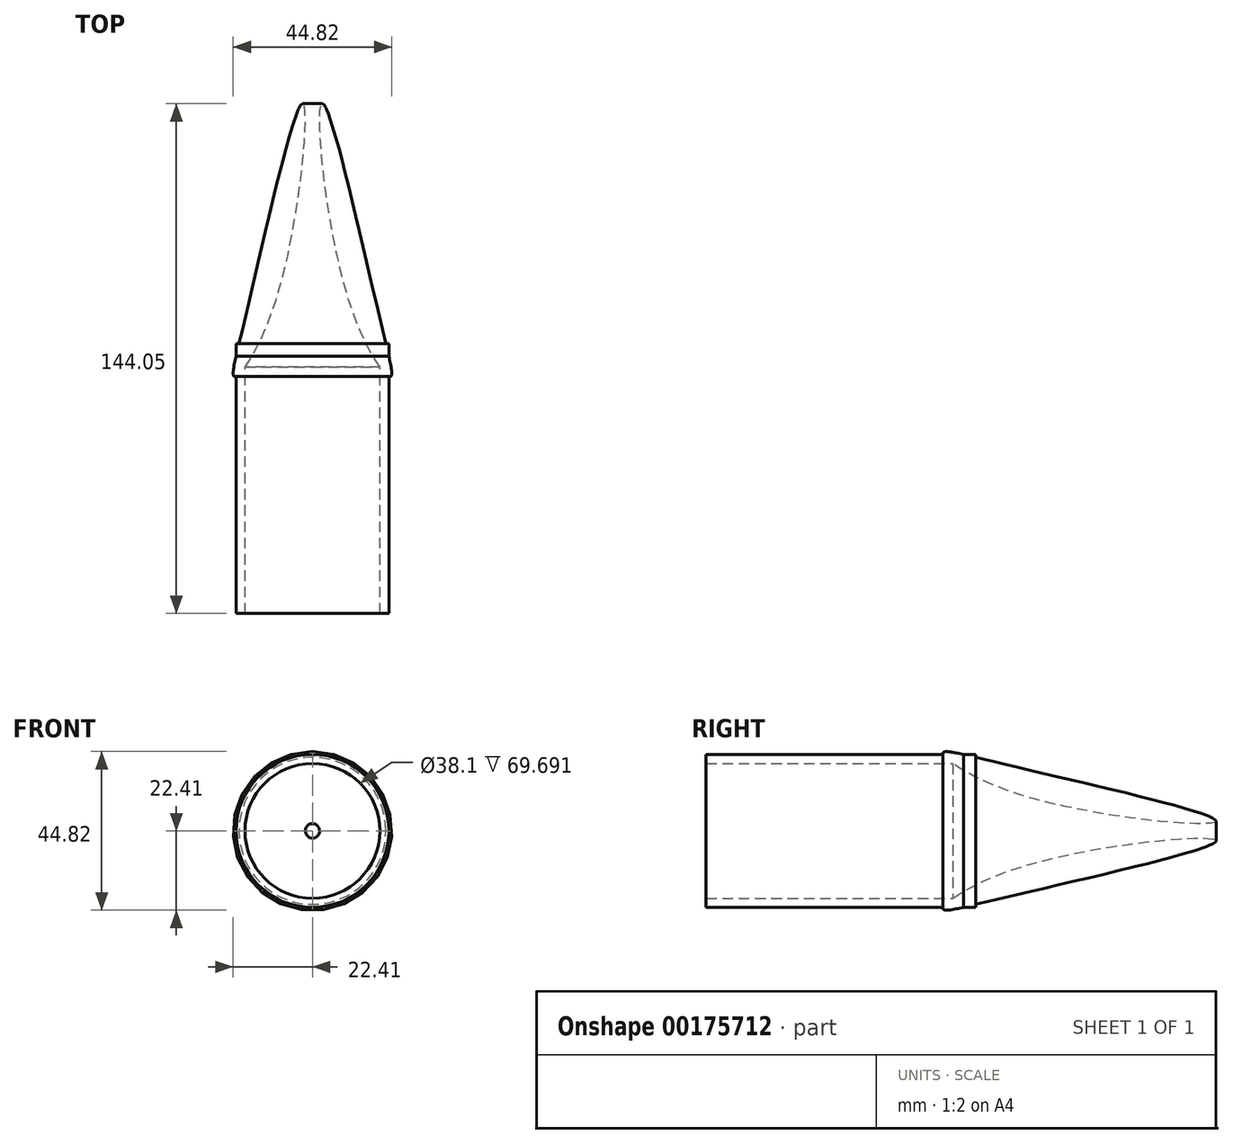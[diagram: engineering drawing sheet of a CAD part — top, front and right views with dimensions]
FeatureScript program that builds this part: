
annotation { "Feature Type Name" : "Feature", "Feature Type Description" : "" }
export const myFeature = defineFeature(function(context is Context, id is Id, definition is map)
    precondition{}
    {
        {
            var Q0;
            Q0=qCreatedBy(makeId("Front.planeOp"),FACE);
            var sketch = newSketch(context, id + "F0", { "sketchPlane" : qUnion([Q0])});
            skCircle(sketch, "E0", {"center": v(0, 0) * mm, "radius": 21.59 * mm});
            skLineSegment(sketch, "E1", {"start": v(-21.59, 0) * mm, "end": v(21.59, 0) * mm});
            skSolve(sketch);
        }
        {
            var Q0;
            {var subQ0=sQuery(id+"F0.wireOp",EDGE,"E1");Q0=makeQuery(id+"F0.imprint","IMPRINT",FACE,{"disambiguationData":[TD([[makeQuery(id+"F0.imprint","IMPRINT",EDGE,{"derivedFrom":subQ0}),-1.0]])]});}
            extrude(context, id + "F1", {"entities" : qUnion([Q0]), "depth" : 76.2 * mm});
        }
        {
            var Q0;
            {var subQ0=sQuery(id+"F0.wireOp",EDGE,"E1");Q0=makeQuery(id+"F0.imprint","IMPRINT",FACE,{"disambiguationData":[TD([[makeQuery(id+"F0.imprint","IMPRINT",EDGE,{"derivedFrom":subQ0}),1.0]])]});}
            extrude(context, id + "F2", {"entities" : qUnion([Q0]), "operationType" : NewBodyOperationType.ADD, "depth" : 76.2 * mm});
        }
        {
            var Q0;
            Q0=qCreatedBy(makeId("Front.planeOp"),FACE);
            var sketch = newSketch(context, id + "F3", { "sketchPlane" : qUnion([Q0])});
            skCircle(sketch, "E2", {"center": v(0, 0) * mm, "radius": 19.05 * mm});
            skSolve(sketch);
        }
        {
            var Q0;
            Q0 = qSketchRegion(id + "F3", true);
            extrude(context, id + "F4", {"entities" : qUnion([Q0]), "operationType" : NewBodyOperationType.REMOVE, "depth" : 76.2 * mm});
        }
        {
            var Q0;
            Q0=qCreatedBy(makeId("Top.planeOp"),FACE);
            var sketch = newSketch(context, id + "F5", { "sketchPlane" : qUnion([Q0])});
            skPoint(sketch, "E3.center.orphan", {"position": v(21.96, 0) * mm});
            skFitSpline(sketch, "E4", {"points": [v(21.96, -9.28) * mm, v(19.52, 5.12) * mm, v(2.88, 67.85) * mm, v(9.92, 13.44) * mm, v(21.96, -9.28) * mm]});
            skSolve(sketch);
        }
        {
            var Q0;
            Q0 = qSketchRegion(id + "F5", true);
            var Q1;
            Q1=sQuery(id+"F0.wireOp",EDGE,"E0");
            revolve(context, id + "F6", {"operationType" : NewBodyOperationType.ADD, "entities" : qUnion([Q0]), "axis" : qUnion([Q1]), "revolveType" : RevolveType.FULL});
        }
    });
